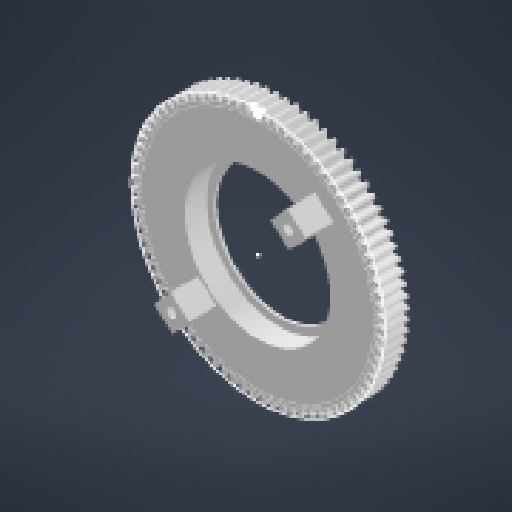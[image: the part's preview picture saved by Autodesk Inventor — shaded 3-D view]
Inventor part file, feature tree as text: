
AUTODESK INVENTOR PART (.ipt)
format: ipt  version: 2023.2 (Build 272271000, 271)  size: 464,384 bytes
history: native  units: mm
features: extrude x5, sketch x3, reference x3, other x3, pattern_circular x1
ambient origin geometry x8: Origin, YZ Plane, XZ Plane, XY Plane, X Axis, Y Axis, Z Axis, Center Point
bodies: Solid1 (feature_tree)
feature tree (15):
  sketch  "Sketch1"  dims[d0=8.0mm d1=0.0mm]
  extrude  "Extrusion1"  TaperAngle=0.0deg  [1 undecoded]
  extrude  "Extrusion2"  Depth=800.0mm TaperAngle=360.0deg
  pattern_circular  "Circular Pattern1"  [2 undecoded]
  sketch  "Sketch2"  dims[d2=0.0mm d3=0.0mm d4=800.0mm d5=360.0deg]
  extrude  "Extrusion3"  TaperAngle=0.0deg  [1 undecoded]
  extrude  "Extrusion4"  Depth=7.0mm TaperAngle=0.0deg
  extrude  "Extrusion5"  Depth=9.0mm TaperAngle=0.0deg
  sketch  "Sketch3"  dims[d7=47.0mm d8=42.0mm d9=0.0mm d10=0.0mm d11=7.0mm d12=0.0mm d13=9.0mm d14=0.0mm]
  reference  "Reference1"
  reference  "Reference2"
  reference  "Reference3"
  parser-record x1  (decoder bookkeeping rows leaked as tree rows — omitted from the tree; the rows remain in map.json)
  other  "turret_assembly.iam"
  other  "vertical_axis_hal_holder:2"
note: 4 required parameter values undecoded (feature->parameter linkage not recoverable at this tier; creation-order binding heuristic only, values carry confidence <= 0.55)
note: 1 file-system path scrubbed to <path> (originals preserved in map.json)
